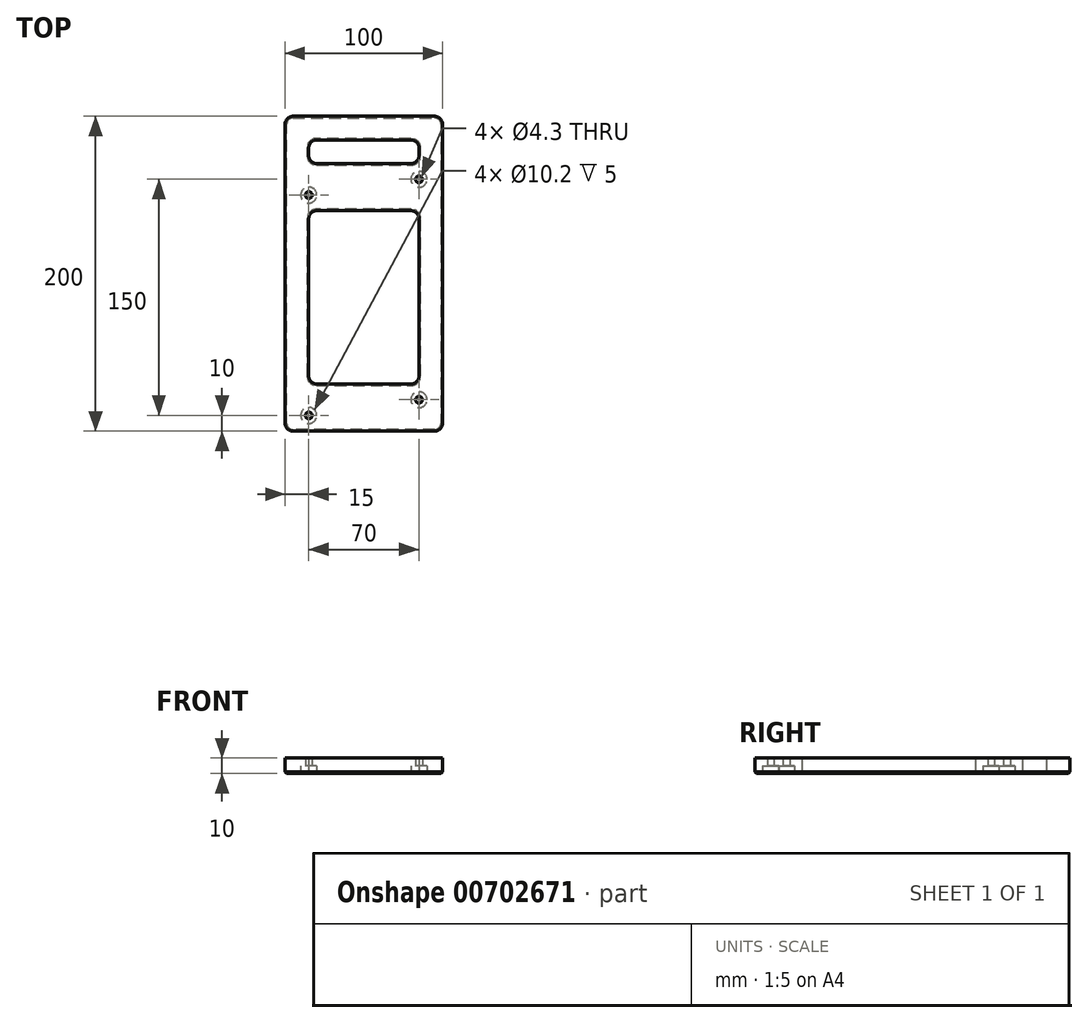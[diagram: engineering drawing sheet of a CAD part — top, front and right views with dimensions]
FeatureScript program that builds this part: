
annotation { "Feature Type Name" : "Feature", "Feature Type Description" : "" }
export const myFeature = defineFeature(function(context is Context, id is Id, definition is map)
    precondition{}
    {
        {
            var Q0;
            Q0=qCreatedBy(makeId("Top.planeOp"),FACE);
            var sketch = newSketch(context, id + "F0", { "sketchPlane" : qUnion([Q0])});
            skLineSegment(sketch, "E0.bottom", {"start": v(50, 100) * mm, "end": v(-50, 100) * mm});
            skLineSegment(sketch, "E0.top", {"start": v(50, -100) * mm, "end": v(-50, -100) * mm});
            skLineSegment(sketch, "E0.left", {"start": v(50, 100) * mm, "end": v(50, -100) * mm});
            skLineSegment(sketch, "E0.right", {"start": v(-50, 100) * mm, "end": v(-50, -100) * mm});
            skPoint(sketch, "E0.middle", {"position": v(0, 0) * mm});
            skCircle(sketch, "E1", {"center": v(-35, 50) * mm, "radius": 2.15 * mm});
            skCircle(sketch, "E2", {"center": v(35, 60) * mm, "radius": 2.15 * mm});
            skCircle(sketch, "E3", {"center": v(-35, -90) * mm, "radius": 2.15 * mm});
            skCircle(sketch, "E4", {"center": v(35, -80) * mm, "radius": 2.15 * mm});
            skLineSegment(sketch, "E5.bottom", {"start": v(-35, -70) * mm, "end": v(35, -70) * mm});
            skLineSegment(sketch, "E5.top", {"start": v(-35, 40) * mm, "end": v(35, 40) * mm});
            skLineSegment(sketch, "E5.left", {"start": v(-35, -70) * mm, "end": v(-35, 40) * mm});
            skLineSegment(sketch, "E5.right", {"start": v(35, -70) * mm, "end": v(35, 40) * mm});
            skLineSegment(sketch, "E6.bottom", {"start": v(-35, 85) * mm, "end": v(35, 85) * mm});
            skLineSegment(sketch, "E6.top", {"start": v(-35, 70) * mm, "end": v(35, 70) * mm});
            skLineSegment(sketch, "E6.left", {"start": v(-35, 85) * mm, "end": v(-35, 70) * mm});
            skLineSegment(sketch, "E6.right", {"start": v(35, 85) * mm, "end": v(35, 70) * mm});
            skCircle(sketch, "E7", {"center": v(-35, 50) * mm, "radius": 5.1 * mm});
            skCircle(sketch, "E8", {"center": v(35, 60) * mm, "radius": 5.1 * mm});
            skCircle(sketch, "E9", {"center": v(-35, -90) * mm, "radius": 5.1 * mm});
            skCircle(sketch, "E10", {"center": v(35, -80) * mm, "radius": 5.1 * mm});
            skSolve(sketch);
        }
        {
            var Q0;
            Q0 = qSketchRegion(id + "F0", true);
            var Q1;
            Q1=makeQuery(id+"F0.imprint","IMPRINT",FACE,{"disambiguationData":[TD([[makeQuery(id+"F0.imprint","IMPRINT",EDGE,{"derivedFrom":sQuery(id+"F0.wireOp",EDGE,"E4")}),-1.0]])]});
            var Q2;
            Q2=makeQuery(id+"F0.imprint","IMPRINT",FACE,{"disambiguationData":[TD([[makeQuery(id+"F0.imprint","IMPRINT",EDGE,{"derivedFrom":sQuery(id+"F0.wireOp",EDGE,"E3")}),-1.0]])]});
            var Q3;
            Q3=makeQuery(id+"F0.imprint","IMPRINT",FACE,{"disambiguationData":[TD([[makeQuery(id+"F0.imprint","IMPRINT",EDGE,{"derivedFrom":sQuery(id+"F0.wireOp",EDGE,"E1")}),-1.0]])]});
            var Q4;
            Q4=makeQuery(id+"F0.imprint","IMPRINT",FACE,{"disambiguationData":[TD([[makeQuery(id+"F0.imprint","IMPRINT",EDGE,{"derivedFrom":sQuery(id+"F0.wireOp",EDGE,"E2")}),-1.0]])]});
            extrude(context, id + "F1", {"entities" : qUnion([Q0, Q1, Q2, Q3, Q4]), "depth" : 10 * mm, "offsetDistance" : 25 * mm});
        }
        {
            var Q0;
            Q0=makeQuery(id+"F1.opExtrude","SWEPT_EDGE",EDGE,{"disambiguationData":[OSD([sQuery(id+"F0.wireOp",EDGE,"E0.top"),sQuery(id+"F0.wireOp",EDGE,"E0.right")])]});
            var Q1;
            Q1=makeQuery(id+"F1.opExtrude","SWEPT_EDGE",EDGE,{"disambiguationData":[OSD([sQuery(id+"F0.wireOp",EDGE,"E0.top"),sQuery(id+"F0.wireOp",EDGE,"E0.left")])]});
            var Q2;
            Q2=makeQuery(id+"F1.opExtrude","SWEPT_EDGE",EDGE,{"disambiguationData":[OSD([sQuery(id+"F0.wireOp",EDGE,"E5.bottom"),sQuery(id+"F0.wireOp",EDGE,"E5.right")])]});
            var Q3;
            Q3=makeQuery(id+"F1.opExtrude","SWEPT_EDGE",EDGE,{"disambiguationData":[OSD([sQuery(id+"F0.wireOp",EDGE,"E5.bottom"),sQuery(id+"F0.wireOp",EDGE,"E5.left")])]});
            var Q4;
            Q4=makeQuery(id+"F1.opExtrude","SWEPT_EDGE",EDGE,{"disambiguationData":[OSD([sQuery(id+"F0.wireOp",EDGE,"E5.top"),sQuery(id+"F0.wireOp",EDGE,"E5.right")])]});
            var Q5;
            Q5=makeQuery(id+"F1.opExtrude","SWEPT_EDGE",EDGE,{"disambiguationData":[OSD([sQuery(id+"F0.wireOp",EDGE,"E5.top"),sQuery(id+"F0.wireOp",EDGE,"E5.left")])]});
            var Q6;
            Q6=makeQuery(id+"F1.opExtrude","SWEPT_EDGE",EDGE,{"disambiguationData":[OSD([sQuery(id+"F0.wireOp",EDGE,"E0.bottom"),sQuery(id+"F0.wireOp",EDGE,"E0.right")])]});
            var Q7;
            Q7=makeQuery(id+"F1.opExtrude","SWEPT_EDGE",EDGE,{"disambiguationData":[OSD([sQuery(id+"F0.wireOp",EDGE,"E0.bottom"),sQuery(id+"F0.wireOp",EDGE,"E0.left")])]});
            var Q8;
            Q8=makeQuery(id+"F1.opExtrude","SWEPT_EDGE",EDGE,{"disambiguationData":[OSD([sQuery(id+"F0.wireOp",EDGE,"E6.top"),sQuery(id+"F0.wireOp",EDGE,"E6.right")])]});
            var Q9;
            Q9=makeQuery(id+"F1.opExtrude","SWEPT_EDGE",EDGE,{"disambiguationData":[OSD([sQuery(id+"F0.wireOp",EDGE,"E6.bottom"),sQuery(id+"F0.wireOp",EDGE,"E6.right")])]});
            var Q10;
            Q10=makeQuery(id+"F1.opExtrude","SWEPT_EDGE",EDGE,{"disambiguationData":[OSD([sQuery(id+"F0.wireOp",EDGE,"E6.top"),sQuery(id+"F0.wireOp",EDGE,"E6.left")])]});
            var Q11;
            Q11=makeQuery(id+"F1.opExtrude","SWEPT_EDGE",EDGE,{"disambiguationData":[OSD([sQuery(id+"F0.wireOp",EDGE,"E6.bottom"),sQuery(id+"F0.wireOp",EDGE,"E6.left")])]});
            fillet(context, id + "F2", {"entities" : qUnion([Q0, Q1, Q2, Q3, Q4, Q5, Q6, Q7, Q8, Q9, Q10, Q11]), "radius" : 5 * mm, "tangentPropagation" : true, "allowEdgeOverflow" : false});
        }
        {
            var Q0;
            Q0=makeQuery(id+"F1.opExtrude","CAP_FACE",FACE,{"disambiguationData":[OSD([sQuery(id+"F0.wireOp",EDGE,"E0.bottom"),sQuery(id+"F0.wireOp",EDGE,"E0.top"),sQuery(id+"F0.wireOp",EDGE,"E0.left"),sQuery(id+"F0.wireOp",EDGE,"E0.right"),sQuery(id+"F0.wireOp",EDGE,"E1"),sQuery(id+"F0.wireOp",EDGE,"E2"),sQuery(id+"F0.wireOp",EDGE,"E3"),sQuery(id+"F0.wireOp",EDGE,"E4"),sQuery(id+"F0.wireOp",EDGE,"E5.bottom"),sQuery(id+"F0.wireOp",EDGE,"E5.top"),sQuery(id+"F0.wireOp",EDGE,"E5.left"),sQuery(id+"F0.wireOp",EDGE,"E5.right"),sQuery(id+"F0.wireOp",EDGE,"E6.bottom"),sQuery(id+"F0.wireOp",EDGE,"E6.top"),sQuery(id+"F0.wireOp",EDGE,"E6.left"),sQuery(id+"F0.wireOp",EDGE,"E6.right")])],"isStart":true});
            chamfer(context, id + "F3", {"entities" : qUnion([Q0]), "width" : 1 * mm, "tangentPropagation" : true});
        }
        {
            var Q0;
            Q0=makeQuery(id+"F0.imprint","IMPRINT",FACE,{"disambiguationData":[TD([[makeQuery(id+"F0.imprint","IMPRINT",EDGE,{"derivedFrom":sQuery(id+"F0.wireOp",EDGE,"E1")}),-1.0]])]});
            var Q1;
            Q1=makeQuery(id+"F0.imprint","IMPRINT",FACE,{"disambiguationData":[TD([[makeQuery(id+"F0.imprint","IMPRINT",EDGE,{"derivedFrom":sQuery(id+"F0.wireOp",EDGE,"E2")}),-1.0]])]});
            var Q2;
            Q2=makeQuery(id+"F0.imprint","IMPRINT",FACE,{"disambiguationData":[TD([[makeQuery(id+"F0.imprint","IMPRINT",EDGE,{"derivedFrom":sQuery(id+"F0.wireOp",EDGE,"E4")}),-1.0]])]});
            var Q3;
            Q3=makeQuery(id+"F0.imprint","IMPRINT",FACE,{"disambiguationData":[TD([[makeQuery(id+"F0.imprint","IMPRINT",EDGE,{"derivedFrom":sQuery(id+"F0.wireOp",EDGE,"E3")}),-1.0]])]});
            extrude(context, id + "F4", {"entities" : qUnion([Q0, Q1, Q2, Q3]), "operationType" : NewBodyOperationType.REMOVE, "depth" : 5 * mm, "offsetDistance" : 25 * mm});
        }
    });
